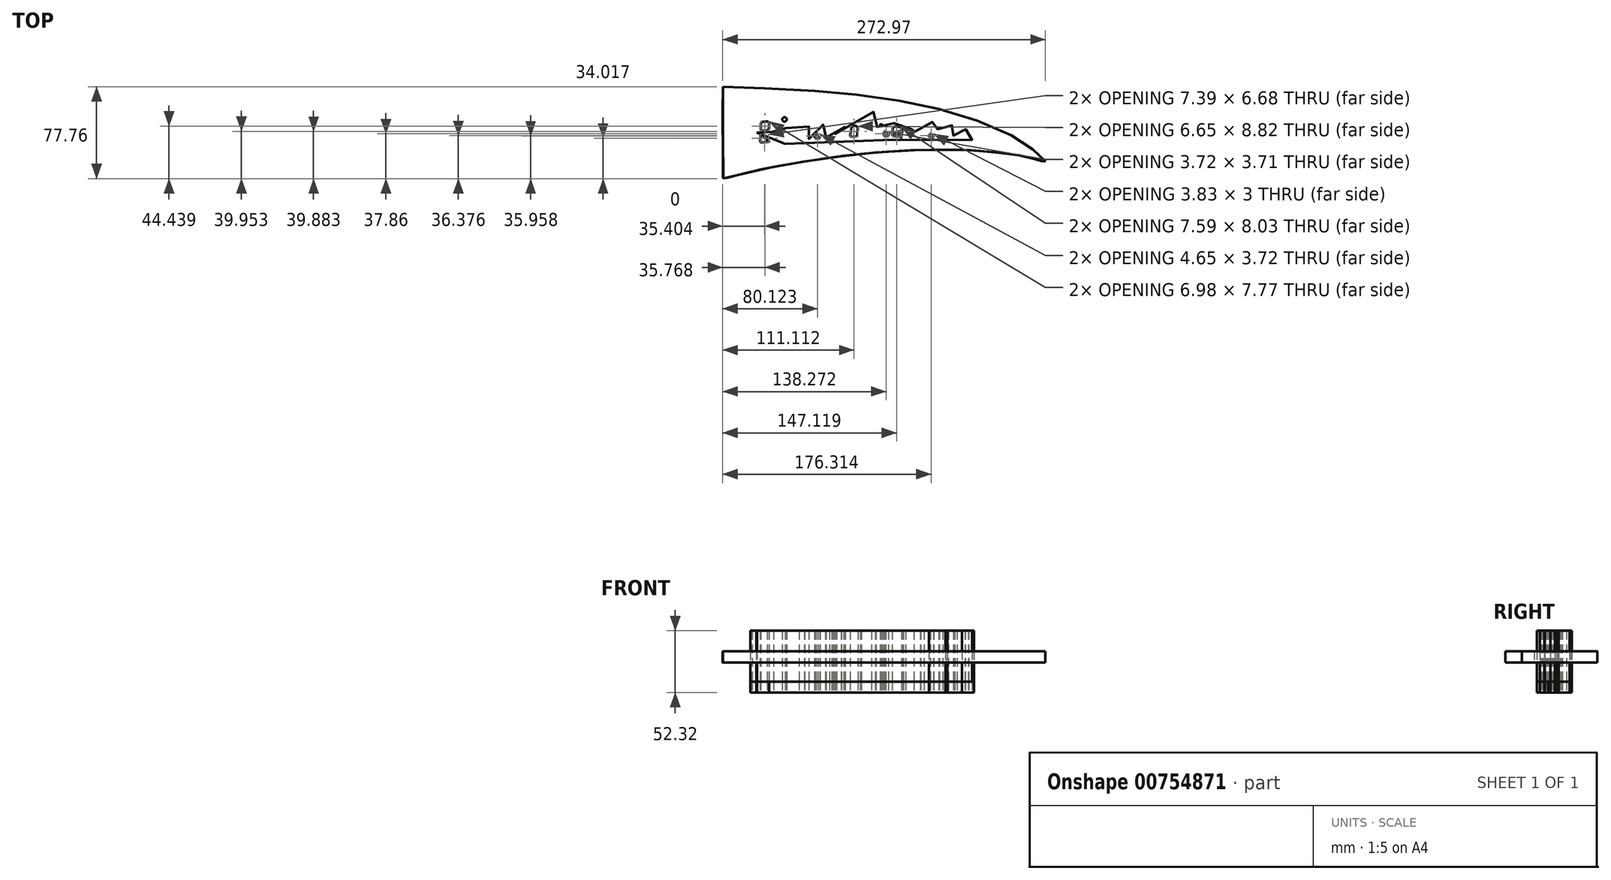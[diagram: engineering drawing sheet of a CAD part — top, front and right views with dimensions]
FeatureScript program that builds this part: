
annotation { "Feature Type Name" : "Feature", "Feature Type Description" : "" }
export const myFeature = defineFeature(function(context is Context, id is Id, definition is map)
    precondition{}
    {
        {
            var Q0;
            Q0=qCreatedBy(makeId("Top.planeOp"),FACE);
            var sketch = newSketch(context, id + "F0", { "sketchPlane" : qUnion([Q0])});
            skFitSpline(sketch, "E0", {"points": [v(-102.23, 14.3) * mm, v(-99.02, 14.5) * mm, v(-97.7, 14.57) * mm, v(-96.73, 14.3) * mm, v(-95.96, 13.11) * mm, v(-95.96, 10.54) * mm, v(-96.17, 8.24) * mm, v(-96.45, 7.54) * mm, v(-97.07, 7.12) * mm, v(-97.9, 6.98) * mm, v(-101.95, 6.7) * mm, v(-102.72, 7.05) * mm, v(-103.06, 7.89) * mm, v(-103.06, 9.21) * mm, v(-102.79, 13.4) * mm, v(-102.23, 14.3) * mm]});
            skFitSpline(sketch, "E1", {"points": [v(-103.41, 2.25) * mm, v(-103.41, 3.22) * mm, v(-102.92, 3.57) * mm, v(-102.3, 3.43) * mm, v(-100.97, 2.1) * mm, v(-96.3, -1.86) * mm, v(-95.96, -2.4) * mm, v(-96.16, -2.7) * mm, v(-96.9, -2.65) * mm, v(-102.61, -3.2) * mm, v(-103.2, -3.04) * mm, v(-103.55, -2.3) * mm, v(-103.55, -1.17) * mm, v(-103.41, 2.25) * mm]});
            skFitSpline(sketch, "E2", {"points": [v(-56.42, 4.05) * mm, v(-55.95, 3.96) * mm, v(-55.25, 3.32) * mm, v(-53.17, 1.41) * mm, v(-52.79, 0.97) * mm, v(-52.79, 0.74) * mm, v(-53.1, 0.56) * mm, v(-56.6, 0.36) * mm, v(-57.03, 0.62) * mm, v(-57.38, 1.06) * mm, v(-57.47, 1.76) * mm, v(-57.47, 2.79) * mm, v(-57.3, 3.32) * mm, v(-56.91, 3.81) * mm, v(-56.42, 4.05) * mm]});
            skFitSpline(sketch, "E3", {"points": [v(-26.33, 9.06) * mm, v(-26.12, 9.68) * mm, v(-25.63, 10.24) * mm, v(-24.9, 10.59) * mm, v(-24, 10.8) * mm, v(-22.36, 10.66) * mm, v(-21.6, 10.31) * mm, v(-21.07, 9.68) * mm, v(-20.83, 8.7) * mm, v(-21, 7.52) * mm, v(-21.63, 2.65) * mm, v(-21.84, 2.25) * mm, v(-22.32, 1.81) * mm, v(-23.27, 1.81) * mm, v(-26.54, 1.85) * mm, v(-27.2, 2.1) * mm, v(-27.51, 2.68) * mm, v(-27.44, 3.55) * mm, v(-26.33, 9.06) * mm]});
            skFitSpline(sketch, "E4", {"points": [v(-1.16, 12.05) * mm, v(-0.54, 12.03) * mm, v(-0.18, 11.72) * mm, v(0, 11.24) * mm, v(-0.16, 10.87) * mm, v(-0.38, 10.67) * mm, v(-0.67, 10.67) * mm, v(-1.76, 11.49) * mm, v(-1.93, 11.72) * mm, v(-1.93, 11.97) * mm, v(-1.68, 12.09) * mm, v(-1.16, 12.05) * mm]});
            skFitSpline(sketch, "E5", {"points": [v(1.15, 4.22) * mm, v(1.3, 5.55) * mm, v(1.38, 5.88) * mm, v(1.57, 6.1) * mm, v(1.83, 6.16) * mm, v(2.32, 5.91) * mm, v(4.4, 4.59) * mm, v(4.76, 4.35) * mm, v(4.86, 4.05) * mm, v(4.86, 3.63) * mm, v(4.9, 2.25) * mm, v(4.83, 2.25) * mm, v(4.5, 2.25) * mm, v(1.81, 2.25) * mm, v(1.34, 2.41) * mm, v(1.15, 2.83) * mm, v(1.14, 3.1) * mm, v(1.1, 3.27) * mm, v(1.15, 4.22) * mm]});
            skFitSpline(sketch, "E6", {"points": [v(12.27, 10.13) * mm, v(14.6, 9.93) * mm, v(15.4, 9.75) * mm, v(15.96, 9.06) * mm, v(16.07, 8.43) * mm, v(15.2, 2.84) * mm, v(14.93, 2.25) * mm, v(14.52, 2.1) * mm, v(13.61, 2.1) * mm, v(9.66, 2.1) * mm, v(8.87, 2.52) * mm, v(8.43, 3.2) * mm, v(8.08, 3.81) * mm, v(8.02, 4.63) * mm, v(8.14, 5.27) * mm, v(8.58, 8.29) * mm, v(8.72, 9.06) * mm, v(8.96, 9.57) * mm, v(9.57, 10.19) * mm, v(10.74, 10.34) * mm, v(12.27, 10.13) * mm]});
            skFitSpline(sketch, "E7", {"points": [v(39.13, 2.33) * mm, v(39.2, 2.87) * mm, v(39.48, 3.4) * mm, v(40.27, 4) * mm, v(40.56, 4.15) * mm, v(40.87, 4.15) * mm, v(41.24, 3.86) * mm, v(42.86, 1.6) * mm, v(43.02, 1.34) * mm, v(42.96, 1.1) * mm, v(42.8, 1.07) * mm, v(40.02, 1.21) * mm, v(39.57, 1.36) * mm, v(39.28, 1.77) * mm, v(39.13, 2.33) * mm]});
            skFitSpline(sketch, "E8", {"points": [v(-106.55, 5.26) * mm, v(-106.1, 12.95) * mm, v(-106.3, 13.34) * mm, v(-106.8, 13.59) * mm, v(-107.54, 13.54) * mm, v(-108.67, 13.54) * mm, v(-109.65, 13.83) * mm, v(-110.1, 14.28) * mm, v(-110.2, 15.21) * mm, v(-109.85, 16.2) * mm, v(-108.58, 16.58) * mm, v(-108.06, 16.61) * mm, v(-94.3, 18.16) * mm, v(-93.2, 18.08) * mm, v(-92.6, 17.7) * mm, v(-92.24, 16.96) * mm, v(-92.36, 15.67) * mm, v(-93, 5.78) * mm, v(-93.73, 4.87) * mm, v(-94.74, 4.21) * mm, v(-96.07, 3.86) * mm, v(-97.25, 3.86) * mm, v(-97.42, 3.86) * mm, v(-96.9, 3.17) * mm, v(-91.26, -1.82) * mm, v(-90.4, -2.17) * mm, v(-89.63, -2.13) * mm, v(-86.04, -1.71) * mm, v(-85.8, -1.44) * mm, v(-85.62, -0.25) * mm, v(-84.7, 10.29) * mm, v(-84.25, 10.83) * mm, v(-83.56, 11.25) * mm, v(-82.75, 11.25) * mm, v(-82.06, 10.88) * mm, v(-81.71, 10.14) * mm, v(-81.67, 9.2) * mm, v(-82.33, 0) * mm, v(-82.28, -0.52) * mm, v(-82, -0.92) * mm, v(-81.55, -1.17) * mm, v(-81.06, -1.17) * mm, v(-80.43, -1.17) * mm, v(-74.56, -0.8) * mm, v(-74.2, -0.65) * mm, v(-74.07, -0.43) * mm, v(-73.98, 0) * mm, v(-73.2, 9.61) * mm, v(-73.08, 10.23) * mm, v(-72.63, 10.89) * mm, v(-72, 11.13) * mm, v(-70.78, 11.38) * mm, v(-63.92, 11.76) * mm, v(-63.16, 11.59) * mm, v(-62.63, 11) * mm, v(-62.46, 10.26) * mm, v(-62.91, 6.19) * mm, v(-63.26, 5.42) * mm, v(-64.2, 5.04) * mm, v(-65.38, 5.21) * mm, v(-65.9, 5.94) * mm, v(-65.94, 7.05) * mm, v(-65.73, 8.35) * mm, v(-66.12, 8.7) * mm, v(-68.66, 8.42) * mm, v(-69.5, 8) * mm, v(-70.02, 7.05) * mm, v(-70.23, 6.15) * mm, v(-70.71, 2.33) * mm, v(-70.64, 1.34) * mm, v(-70.26, 0.62) * mm, v(-69.63, 0) * mm, v(-69.04, -0.29) * mm, v(-68.24, -0.43) * mm, v(-62.63, -0.25) * mm, v(-61.48, 0) * mm, v(-60.9, 0.72) * mm, v(-60.61, 1.8) * mm, v(-60.44, 2.98) * mm, v(-57.9, 20.73) * mm, v(-57.24, 21.6) * mm, v(-56.16, 21.8) * mm, v(-55.17, 21.35) * mm, v(-54.8, 20.35) * mm, v(-54.92, 19.28) * mm, v(-56.4, 9.21) * mm, v(-56.27, 8.3) * mm, v(-55.88, 8) * mm, v(-55.26, 8.2) * mm, v(-54.6, 8.7) * mm, v(-50.66, 11.72) * mm, v(-50.17, 12.1) * mm, v(-49.54, 12.28) * mm, v(-46.55, 12.45) * mm, v(-45.71, 12.31) * mm, v(-45.23, 11.93) * mm, v(-44.88, 11.13) * mm, v(-44.88, 10.36) * mm, v(-45.3, 7.05) * mm, v(-45.78, 6.4) * mm, v(-46.9, 6.05) * mm, v(-47.9, 6.4) * mm, v(-48.3, 7.05) * mm, v(-48.19, 8.07) * mm, v(-47.94, 8.55) * mm, v(-47.87, 8.8) * mm, v(-48.74, 9.46) * mm, v(-49.13, 9.5) * mm, v(-53.13, 6.29) * mm, v(-53.17, 5.94) * mm, v(-52.85, 5.45) * mm, v(-47.85, 1) * mm, v(-47.48, 0.88) * mm, v(-43.71, 1) * mm, v(-43.13, 1.34) * mm, v(-42.88, 2.1) * mm, v(-42.88, 3.86) * mm, v(-42.68, 4.82) * mm, v(-41.93, 5.52) * mm, v(-40.98, 5.98) * mm, v(-41.56, 6.52) * mm, v(-42.01, 7.05) * mm, v(-41.97, 7.47) * mm, v(-41.06, 12.19) * mm, v(-40.15, 13.06) * mm, v(-39.36, 13.35) * mm, v(-37.5, 13.35) * mm, v(-36.4, 13.4) * mm, v(-33.2, 13.5) * mm, v(-32.16, 13.25) * mm, v(-31.62, 12.07) * mm, v(-32.01, 9.9) * mm, v(-32.75, 9.01) * mm, v(-33.54, 8.87) * mm, v(-34.67, 9.16) * mm, v(-34.87, 9.5) * mm, v(-34.87, 10.3) * mm, v(-35.26, 10.84) * mm, v(-36.35, 10.74) * mm, v(-37.68, 10.59) * mm, v(-38.41, 10.15) * mm, v(-38.7, 9.26) * mm, v(-38.86, 8.52) * mm, v(-38.46, 7.93) * mm, v(-37.58, 7.68) * mm, v(-34.28, 7.73) * mm, v(-33.14, 7.73) * mm, v(-32.8, 7.49) * mm, v(-32.9, 5.96) * mm, v(-33.1, 5.27) * mm, v(-33.93, 4.93) * mm, v(-38.51, 4.88) * mm, v(-39.5, 4.68) * mm, v(-39.9, 3.86) * mm, v(-40.09, 3.32) * mm, v(-39.94, 2.33) * mm, v(-39.3, 1.34) * mm, v(-38.27, 1.34) * mm, v(-36, 1.34) * mm, v(-33.1, 1.34) * mm, v(-30.93, 2.1) * mm, v(-30.29, 3.32) * mm, v(-29.8, 5.91) * mm, v(-28.47, 13.35) * mm, v(-28.02, 14.18) * mm, v(-27.09, 14.48) * mm, v(-26.4, 14.33) * mm, v(-26.2, 13.84) * mm, v(-26.05, 12.95) * mm, v(-25.95, 12.36) * mm, v(-25.7, 12.26) * mm, v(-25.36, 13) * mm, v(-24.87, 13.35) * mm, v(-20.1, 13.74) * mm, v(-19.01, 13.4) * mm, v(-18.12, 12.26) * mm, v(-17.83, 11.13) * mm, v(-17.83, 9.95) * mm, v(-18.76, 3.86) * mm, v(-18.42, 2.33) * mm, v(-17.78, 2.33) * mm, v(-15.76, 2.1) * mm, v(-12.9, 2.33) * mm, v(-12.31, 3.86) * mm, v(-10.19, 14.41) * mm, v(-8.96, 20.67) * mm, v(-8.56, 22) * mm, v(-7.33, 22.64) * mm, v(-6.3, 22.05) * mm, v(-6, 21.06) * mm, v(-6.35, 19.14) * mm, v(-9.36, 4.47) * mm, v(-9.07, 3.86) * mm, v(-8.72, 2.94) * mm, v(-7.84, 2.33) * mm, v(-6.7, 2.33) * mm, v(-4.24, 2.33) * mm, v(-2.86, 2.33) * mm, v(-2.17, 3.32) * mm, v(-1.34, 4.86) * mm, v(-1.14, 6.1) * mm, v(-1.09, 7.05) * mm, v(-1.39, 8.06) * mm, v(-2.47, 8.7) * mm, v(-4.14, 9.68) * mm, v(-5.32, 10.67) * mm, v(-5.57, 11.7) * mm, v(-5.37, 12.64) * mm, v(-4.54, 13.58) * mm, v(-3.55, 13.73) * mm, v(1.05, 13.9) * mm, v(1.83, 13.71) * mm, v(2.68, 13.12) * mm, v(2.71, 12.35) * mm, v(2.53, 11.46) * mm, v(2.34, 10.6) * mm, v(2.16, 9.68) * mm, v(2.16, 9.32) * mm, v(2.75, 8.98) * mm, v(5.26, 7.43) * mm, v(5.6, 7.54) * mm, v(6.04, 8.1) * mm, v(6.52, 11.05) * mm, v(6.93, 12.16) * mm, v(7.44, 12.83) * mm, v(8.15, 13.12) * mm, v(15.13, 12.94) * mm, v(15.69, 12.68) * mm, v(16.39, 12.12) * mm, v(16.87, 12.27) * mm, v(16.83, 12.72) * mm, v(16.94, 13.5) * mm, v(17.35, 13.71) * mm, v(19.12, 13.6) * mm, v(19.53, 13.38) * mm, v(19.6, 12.83) * mm, v(19.45, 11.6) * mm, v(18.27, 5.55) * mm, v(17.79, 3.32) * mm, v(18.16, 2.1) * mm, v(19.56, 2.1) * mm, v(22.44, 2.1) * mm, v(23.13, 2.1) * mm, v(23.48, 2.33) * mm, v(23.76, 3.32) * mm, v(25.45, 11.42) * mm, v(25.81, 12.46) * mm, v(26.5, 12.88) * mm, v(27.43, 12.93) * mm, v(34.23, 12.41) * mm, v(34.8, 12.05) * mm, v(35.22, 11.52) * mm, v(35.22, 10.8) * mm, v(34.54, 7.05) * mm, v(34.07, 6.16) * mm, v(32.76, 6.16) * mm, v(31.93, 7.05) * mm, v(32.24, 8.43) * mm, v(32.3, 9.68) * mm, v(31.4, 9.68) * mm, v(28.8, 9.68) * mm, v(28.11, 9.07) * mm, v(27.8, 8.02) * mm, v(27.38, 6.16) * mm, v(26.8, 3.32) * mm, v(26.75, 2.33) * mm, v(27.28, 2.1) * mm, v(27.9, 1.34) * mm, v(28.74, 1.34) * mm, v(35.69, 1.34) * mm, v(36.16, 2.1) * mm, v(37.41, 7.05) * mm, v(39.7, 16) * mm, v(40.53, 18.98) * mm, v(41.24, 20.08) * mm, v(42.1, 20.47) * mm, v(43.02, 20) * mm, v(43.47, 19.02) * mm, v(43.02, 17.62) * mm, v(40.79, 9.36) * mm, v(40.66, 8.78) * mm, v(40.88, 8.43) * mm, v(41.58, 8.43) * mm, v(43.02, 9.36) * mm, v(45.58, 11.07) * mm, v(46.94, 11.25) * mm, v(49.75, 10.8) * mm, v(50.55, 10.5) * mm, v(50.8, 10.13) * mm, v(50.94, 9.27) * mm, v(50.77, 8.43) * mm, v(50.06, 5.27) * mm, v(49.23, 4.05) * mm, v(48.4, 4.05) * mm, v(47.56, 4.92) * mm, v(47.6, 6.16) * mm, v(47.87, 7.05) * mm, v(48.04, 7.55) * mm, v(46.85, 8.08) * mm, v(45.89, 7.82) * mm, v(43.51, 6.16) * mm, v(43.34, 5.8) * mm, v(43.65, 5.44) * mm, v(45.93, 2.98) * mm, v(47.7, 0.72) * mm, v(51.73, 0.46) * mm, v(52.4, 1.34) * mm, v(52.58, 2.1) * mm, v(52.69, 3.32) * mm, v(53.28, 4.05) * mm, v(54.2, 4.6) * mm, v(54.24, 4.9) * mm, v(53.17, 5.64) * mm, v(53.17, 6.16) * mm, v(54.13, 10.13) * mm, v(54.43, 11.03) * mm, v(55.16, 11.4) * mm, v(57.42, 11.44) * mm, v(61.67, 11) * mm, v(62.78, 10.59) * mm, v(63.22, 9.68) * mm, v(62.92, 8.78) * mm, v(62.33, 6.7) * mm, v(61.67, 6.16) * mm, v(60.78, 6.16) * mm, v(60.08, 7.05) * mm, v(60.04, 7.85) * mm, v(59.64, 8.43) * mm, v(57.3, 8.43) * mm, v(56.38, 8.43) * mm, v(56.01, 7.05) * mm, v(55.9, 6.16) * mm, v(56.83, 5.82) * mm, v(59.23, 5.64) * mm, v(60.49, 5.41) * mm, v(61, 4.93) * mm, v(60.86, 4.05) * mm, v(60.3, 2.68) * mm, v(59.6, 2.68) * mm, v(58.16, 2.94) * mm, v(56.64, 3.32) * mm, v(55.6, 2.94) * mm, v(55.2, 2.33) * mm, v(54.98, 1.34) * mm, v(55.2, 0.5) * mm, v(56.72, 0) * mm, v(63.44, -0.31) * mm, v(64.33, 0) * mm, v(64.7, 1.72) * mm, v(66.38, 7.73) * mm, v(67.04, 10.13) * mm, v(68.1, 10.85) * mm, v(69.37, 10.63) * mm, v(69.98, 9.68) * mm, v(69.72, 8.87) * mm, v(69.68, 8.43) * mm, v(70.12, 8.08) * mm, v(70.42, 8.43) * mm, v(71.7, 9.68) * mm, v(72.62, 9.68) * mm, v(75.17, 9.18) * mm, v(75.6, 8.43) * mm, v(75.52, 6.16) * mm, v(74.86, 4.65) * mm, v(73.5, 4.6) * mm, v(72.75, 5.3) * mm, v(72.84, 6.16) * mm, v(72.53, 6.63) * mm, v(71.79, 6.16) * mm, v(68.45, 3.32) * mm, v(67.96, 2.33) * mm, v(67.35, 1) * mm, v(67.44, 0) * mm, v(68, -0.58) * mm, v(69.72, -0.67) * mm, v(76.27, -1.17) * mm, v(77.2, -1.63) * mm, v(77.41, -2.82) * mm, v(76.97, -3.87) * mm, v(76.08, -4.52) * mm, v(73.65, -4.27) * mm, v(67.69, -3.71) * mm, v(52.9, -2.65) * mm, v(42.08, -1.9) * mm, v(22.63, -1.17) * mm, v(-3.34, -0.62) * mm, v(-15.86, -0.68) * mm, v(-28.69, -1.17) * mm, v(-47.04, -2.08) * mm, v(-62.7, -3.2) * mm, v(-80.1, -4.31) * mm, v(-94.67, -5.52) * mm, v(-105.09, -6.63) * mm, v(-109.6, -7.08) * mm, v(-111.19, -7.19) * mm, v(-111.67, -7.04) * mm, v(-111.81, -6.49) * mm, v(-111.74, -4.5) * mm, v(-111.37, -3.94) * mm, v(-110.34, -3.79) * mm, v(-108.12, -3.79) * mm, v(-107.23, -3.38) * mm, v(-106.83, -2.68) * mm, v(-106.83, -1.8) * mm, v(-106.8, 1.34) * mm, v(-106.55, 5.26) * mm]});
            skSolve(sketch);
        }
        {
            var Q0;
            Q0=qCreatedBy(makeId("Top.planeOp"),FACE);
            var sketch = newSketch(context, id + "F1", { "sketchPlane" : qUnion([Q0])});
            skCircle(sketch, "E9", {"center": v(-82.94, 16.27) * mm, "radius": 1.84 * mm});
            skSolve(sketch);
        }
        {
            var Q0;
            Q0=makeQuery(id+"F0.imprint","IMPRINT",FACE,{"disambiguationData":[TD([[makeQuery(id+"F0.imprint","IMPRINT",EDGE,{"derivedFrom":sQuery(id+"F0.wireOp",EDGE,"E0")}),1.0]])]});
            var Q1;
            Q1=makeQuery(id+"F1.imprint","IMPRINT",FACE,{"disambiguationData":[TD([[makeQuery(id+"F1.imprint","IMPRINT",EDGE,{"derivedFrom":sQuery(id+"F1.wireOp",EDGE,"E9")}),1.0]])]});
            extrude(context, id + "F2", {"entities" : qUnion([Q0, Q1]), "depth" : 9.4 * mm, "offsetDistance" : 25.4 * mm});
        }
        {
            var Q0;
            Q0=qCreatedBy(makeId("Top.planeOp"),FACE);
            cPlane(context, id + "F3", {"entities" : qUnion([Q0]), "cplaneType" : CPlaneType.OFFSET, "offset" : 25.4 * mm, "width" : 152.4 * mm, "height" : 152.4 * mm});
        }
        {
            var Q0;
            Q0=qCreatedBy(id+"F3.planeOp",FACE);
            var sketch = newSketch(context, id + "F4", { "sketchPlane" : qUnion([Q0])});
            skFitSpline(sketch, "E10", {"points": [v(-134.92, 43.98) * mm, v(-92.03, 42.4) * mm, v(-42.63, 39.06) * mm, v(-3.08, 34.84) * mm, v(36.87, 27.7) * mm, v(68.8, 19.12) * mm, v(103.58, 5.4) * mm, v(116.88, -2) * mm, v(130.48, -11.6) * mm, v(136.98, -17.82) * mm, v(137.43, -18.23) * mm, v(137.65, -18.74) * mm, v(137.66, -19.24) * mm, v(137.28, -19.68) * mm, v(136.69, -19.72) * mm, v(136.11, -19.52) * mm, v(132.18, -18.23) * mm, v(124.2, -15.94) * mm, v(116.8, -14.16) * mm, v(108.16, -12.98) * mm, v(98.7, -11.87) * mm, v(82.88, -10.32) * mm, v(66.8, -9.4) * mm, v(50.76, -9.34) * mm, v(30.44, -9.52) * mm, v(-3, -11.52) * mm, v(-33.2, -14.56) * mm, v(-60.9, -18.53) * mm, v(-87.87, -23) * mm, v(-111.86, -28.09) * mm, v(-131.12, -32.94) * mm, v(-133.45, -33.64) * mm, v(-134.2, -33.77) * mm, v(-134.68, -33.5) * mm, v(-134.94, -32.89) * mm, v(-134.94, -32.05) * mm, v(-135.19, 43.73) * mm, v(-135.11, 43.98) * mm, v(-134.92, 43.98) * mm]});
            skSolve(sketch);
        }
        {
            var Q0;
            Q0=makeQuery(id+"F4.imprint","IMPRINT",FACE,{"disambiguationData":[TD([[makeQuery(id+"F4.imprint","IMPRINT",EDGE,{"derivedFrom":sQuery(id+"F4.wireOp",EDGE,"E10")}),-1.0]])]});
            extrude(context, id + "F5", {"entities" : qUnion([Q0]), "depth" : 9.65 * mm, "offsetDistance" : 25.4 * mm});
        }
        {
            var Q0;
            Q0=makeQuery(id+"F2.opExtrude","CAP_FACE",FACE,{"disambiguationData":[OSD([sQuery(id+"F0.wireOp",EDGE,"E0"),sQuery(id+"F0.wireOp",EDGE,"E1"),sQuery(id+"F0.wireOp",EDGE,"E2"),sQuery(id+"F0.wireOp",EDGE,"E3"),sQuery(id+"F0.wireOp",EDGE,"E4"),sQuery(id+"F0.wireOp",EDGE,"E5"),sQuery(id+"F0.wireOp",EDGE,"E6"),sQuery(id+"F0.wireOp",EDGE,"E7"),sQuery(id+"F0.wireOp",EDGE,"E8")])],"isStart":false});
            var Q1;
            Q1=makeQuery(id+"F2.opExtrude","CAP_FACE",FACE,{"disambiguationData":[OSD([sQuery(id+"F1.wireOp",EDGE,"E9")])],"isStart":false});
            extrude(context, id + "F6", {"entities" : qUnion([Q0, Q1]), "depth" : 42.93 * mm, "offsetDistance" : 25.4 * mm});
        }
    });
